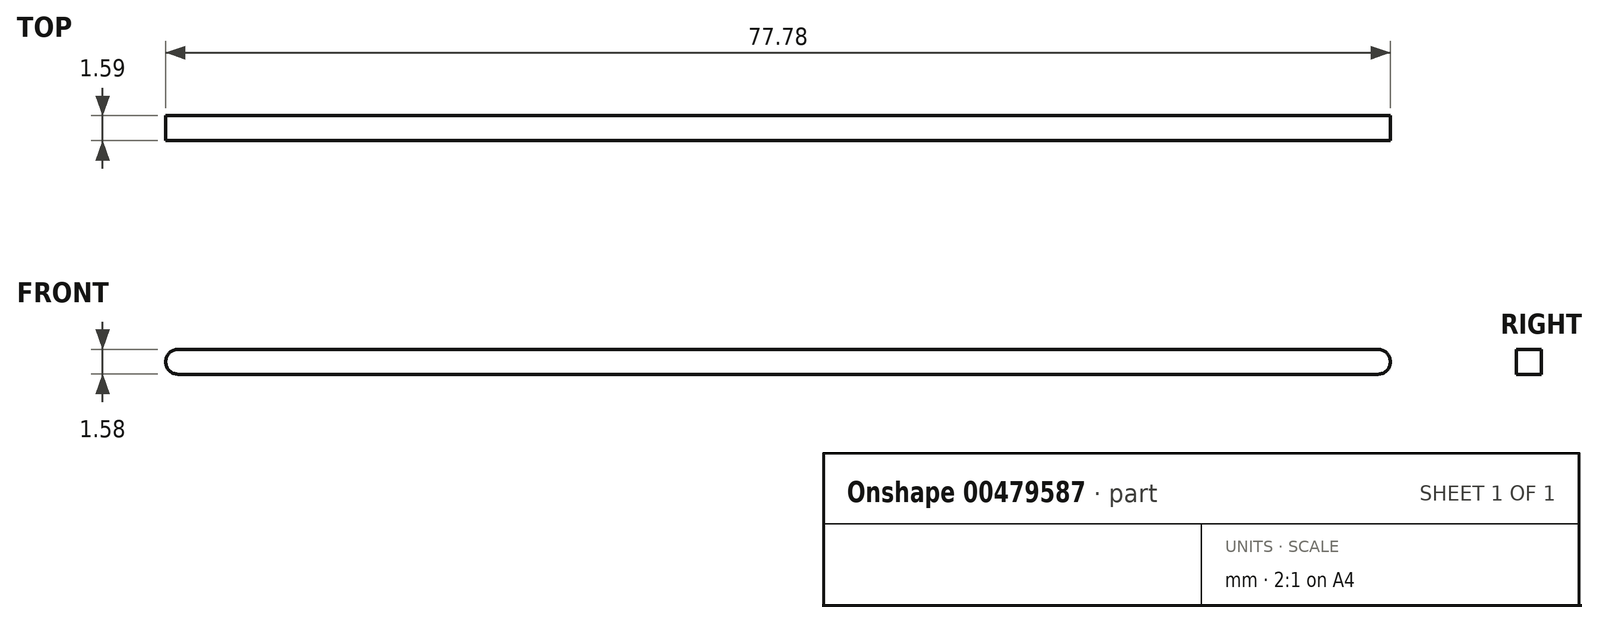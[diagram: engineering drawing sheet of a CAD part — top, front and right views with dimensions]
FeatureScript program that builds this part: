
annotation { "Feature Type Name" : "Feature", "Feature Type Description" : "" }
export const myFeature = defineFeature(function(context is Context, id is Id, definition is map)
    precondition{}
    {
        {
            var Q0;
            Q0=qCreatedBy(makeId("Front.planeOp"),FACE);
            var sketch = newSketch(context, id + "F0", { "sketchPlane" : qUnion([Q0])});
            skLineSegment(sketch, "E0.bottom", {"start": v(38.1, -0.8) * mm, "end": v(-38.1, -0.8) * mm});
            skLineSegment(sketch, "E0.top", {"start": v(38.1, 0.8) * mm, "end": v(-38.1, 0.8) * mm});
            skPoint(sketch, "E0.middle", {"position": v(0, 0) * mm});
            skArc(sketch, "E1", {"start": v(38.1, -0.8) * mm, "mid": v(38.9, 0) * mm, "end": v(38.1, 0.8) * mm});
            skArc(sketch, "E2", {"start": v(-38.1, 0.8) * mm, "mid": v(-38.9, 0) * mm, "end": v(-38.1, -0.8) * mm});
            skSolve(sketch);
        }
        {
            var Q0;
            Q0=makeQuery(id+"F0.imprint","IMPRINT",FACE,{"disambiguationData":[TD([[makeQuery(id+"F0.imprint","IMPRINT",EDGE,{"derivedFrom":sQuery(id+"F0.wireOp",EDGE,"E0.bottom")}),-1.0]])]});
            extrude(context, id + "F1", {"entities" : qUnion([Q0]), "depth" : 1.59 * mm});
        }
    });
